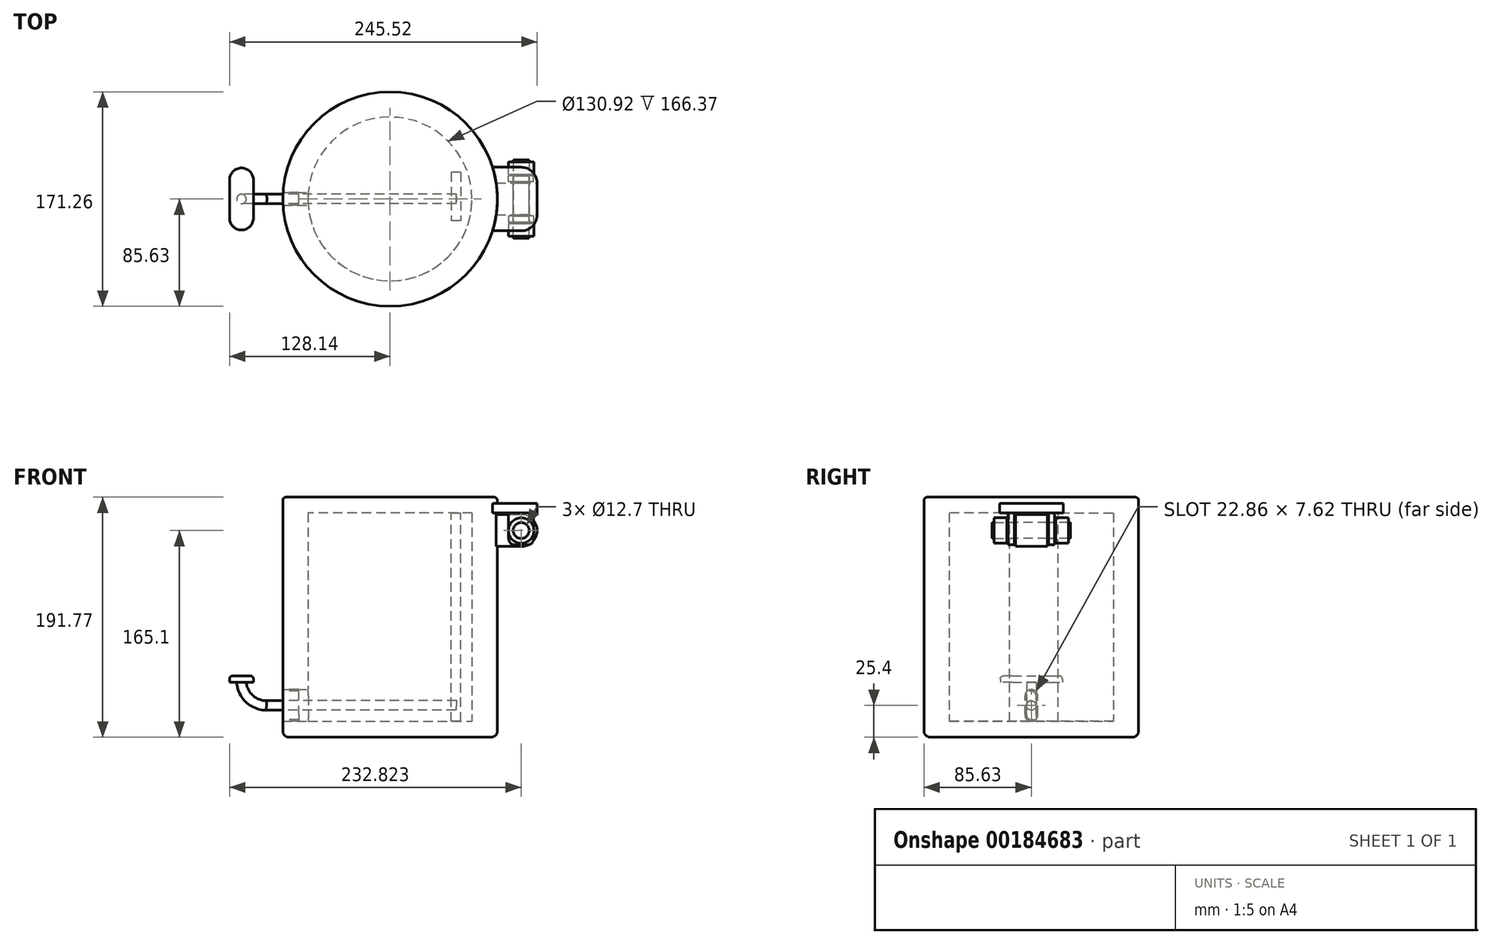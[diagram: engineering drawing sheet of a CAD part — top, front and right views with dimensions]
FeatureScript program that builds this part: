
annotation { "Feature Type Name" : "Feature", "Feature Type Description" : "" }
export const myFeature = defineFeature(function(context is Context, id is Id, definition is map)
    precondition{}
    {
        {
            var Q0;
            Q0=qCreatedBy(makeId("Top.planeOp"),FACE);
            var sketch = newSketch(context, id + "F0", { "sketchPlane" : qUnion([Q0])});
            skCircle(sketch, "E0", {"center": v(0, 0) * mm, "radius": 85.63 * mm});
            skCircle(sketch, "E1", {"center": v(0, 0) * mm, "radius": 65.46 * mm});
            skSolve(sketch);
        }
        {
            var Q0;
            Q0 = qSketchRegion(id + "F0", true);
            extrude(context, id + "F1", {"entities" : qUnion([Q0]), "depth" : 177.8 * mm});
        }
        {
            var Q0;
            Q0=makeQuery(id+"F0.imprint","IMPRINT",FACE,{"disambiguationData":[TD([[makeQuery(id+"F0.imprint","IMPRINT",EDGE,{"derivedFrom":sQuery(id+"F0.wireOp",EDGE,"E0")}),1.0]])]});
            var Q1;
            Q1=makeQuery(id+"F0.imprint","IMPRINT",FACE,{"disambiguationData":[TD([[makeQuery(id+"F0.imprint","IMPRINT",EDGE,{"derivedFrom":sQuery(id+"F0.wireOp",EDGE,"E1")}),1.0]])]});
            extrude(context, id + "F2", {"entities" : qUnion([Q0, Q1]), "operationType" : NewBodyOperationType.ADD, "depth" : 12.7 * mm});
        }
        {
            var Q0;
            Q0=makeQuery(id+"F1.opExtrude","CAP_FACE",FACE,{"disambiguationData":[OSD([sQuery(id+"F0.wireOp",EDGE,"E0"),sQuery(id+"F0.wireOp",EDGE,"E1")])],"isStart":false});
            var sketch = newSketch(context, id + "F3", { "sketchPlane" : qUnion([Q0])});
            skCircle(sketch, "E2.0", {"center": v(0, 0) * mm, "radius": 85.63 * mm});
            skCircle(sketch, "E2.1", {"center": v(0, 0) * mm, "radius": 65.46 * mm});
            skSolve(sketch);
        }
        {
            var Q0;
            Q0 = qSketchRegion(id + "F3", true);
            extrude(context, id + "F4", {"entities" : qUnion([Q0]), "depth" : 1.27 * mm});
        }
        {
            var Q0;
            Q0=makeQuery(id+"F4.opExtrude","CAP_FACE",FACE,{"disambiguationData":[OSD([sQuery(id+"F3.wireOp",EDGE,"E2.0"),sQuery(id+"F3.wireOp",EDGE,"E2.1")])],"isStart":false});
            var sketch = newSketch(context, id + "F5", { "sketchPlane" : qUnion([Q0])});
            skCircle(sketch, "E3.0", {"center": v(0, 0) * mm, "radius": 85.63 * mm});
            skSolve(sketch);
        }
        {
            var Q0;
            Q0 = qSketchRegion(id + "F5", true);
            extrude(context, id + "F6", {"entities" : qUnion([Q0]), "depth" : 12.7 * mm});
        }
        {
            var Q0;
            Q0=makeQuery(id+"F6.opExtrude","CAP_EDGE",EDGE,{"disambiguationData":[OSD([sQuery(id+"F5.wireOp",EDGE,"E3.0")])],"isStart":false});
            fillet(context, id + "F7", {"entities" : qUnion([Q0]), "radius" : 2.54 * mm, "tangentPropagation" : true, "allowEdgeOverflow" : false});
        }
        {
            var Q0;
            Q0=makeQuery(id+"F1.opExtrude","CAP_EDGE",EDGE,{"disambiguationData":[OSD([sQuery(id+"F0.wireOp",EDGE,"E0")])],"isStart":true});
            fillet(context, id + "F8", {"entities" : qUnion([Q0]), "radius" : 5.08 * mm, "tangentPropagation" : true, "allowEdgeOverflow" : false});
        }
        {
            var Q0;
            Q0=makeQuery(id+"F6.opExtrude","CAP_FACE",FACE,{"disambiguationData":[OSD([sQuery(id+"F5.wireOp",EDGE,"E3.0")])],"isStart":true});
            var sketch = newSketch(context, id + "F9", { "sketchPlane" : qUnion([Q0])});
            skLineSegment(sketch, "E4.bottom", {"start": v(48.96, 17.22) * mm, "end": v(56.36, 17.22) * mm});
            skLineSegment(sketch, "E4.top", {"start": v(48.96, -21.27) * mm, "end": v(56.36, -21.27) * mm});
            skLineSegment(sketch, "E4.left", {"start": v(48.96, 17.22) * mm, "end": v(48.96, -21.27) * mm});
            skLineSegment(sketch, "E4.right", {"start": v(56.36, 17.22) * mm, "end": v(56.36, -21.27) * mm});
            skSolve(sketch);
        }
        {
            var Q0;
            Q0 = qSketchRegion(id + "F9", true);
            extrude(context, id + "F10", {"entities" : qUnion([Q0]), "endBound" : BoundingType.UP_TO_NEXT, "depth" : 132.08 * mm});
        }
        {
            var Q0;
            Q0=qCreatedBy(makeId("Right.planeOp"),FACE);
            var sketch = newSketch(context, id + "F11", { "sketchPlane" : qUnion([Q0])});
            skLineSegment(sketch, "E5.0", {"start": v(-85.63, 179.07) * mm, "end": v(85.63, 179.07) * mm});
            skLineSegment(sketch, "E5.1", {"start": v(-85.63, 177.8) * mm, "end": v(85.63, 177.8) * mm});
            skLineSegment(sketch, "E6", {"start": v(0, 45.64) * mm, "end": v(0, -59.13) * mm});
            skPoint(sketch, "E6.startSnap0", {"position": v(0, 177.8) * mm});
            skLineSegment(sketch, "E7.bottom", {"start": v(-5.08, 17.78) * mm, "end": v(5.08, 17.78) * mm});
            skLineSegment(sketch, "E7.top", {"start": v(-5.08, 33.02) * mm, "end": v(5.08, 33.02) * mm});
            skLineSegment(sketch, "E7.left", {"start": v(-5.08, 17.78) * mm, "end": v(-5.08, 33.02) * mm});
            skLineSegment(sketch, "E7.right", {"start": v(5.08, 17.78) * mm, "end": v(5.08, 33.02) * mm});
            skPoint(sketch, "E7.middle", {"position": v(0, 25.4) * mm});
            skArc(sketch, "E8", {"start": v(5.08, 33.02) * mm, "mid": v(0, 38.1) * mm, "end": v(-5.08, 33.02) * mm});
            skArc(sketch, "E9", {"start": v(-5.08, 17.78) * mm, "mid": v(0, 12.7) * mm, "end": v(5.08, 17.78) * mm});
            skSolve(sketch);
        }
        {
            var Q0;
            Q0 = qSketchRegion(id + "F11", true);
            extrude(context, id + "F12", {"entities" : qUnion([Q0]), "operationType" : NewBodyOperationType.REMOVE, "endBound" : BoundingType.THROUGH_ALL, "oppositeDirection" : true, "depth" : 25.4 * mm});
        }
        {
            var Q0;
            Q0=qCreatedBy(makeId("Front.planeOp"),FACE);
            var sketch = newSketch(context, id + "F13", { "sketchPlane" : qUnion([Q0])});
            skFitSpline(sketch, "E10.0", {"points": [v(-85.48, 17.78) * mm, v(-85.48, 17.78) * mm, v(-85.48, 17.72) * mm, v(-85.46, 17.52) * mm, v(-85.44, 17.23) * mm, v(-85.41, 16.75) * mm, v(-85.37, 16.08) * mm, v(-85.34, 15.47) * mm, v(-85.32, 14.97) * mm, v(-85.3, 14.43) * mm, v(-85.28, 13.87) * mm, v(-85.27, 13.28) * mm, v(-85.26, 12.67) * mm, v(-85.25, 12.06) * mm, v(-85.25, 11.44) * mm, v(-85.25, 10.81) * mm, v(-85.26, 9.98) * mm, v(-85.27, 9.2) * mm, v(-85.3, 8.43) * mm, v(-85.32, 7.9) * mm, v(-85.34, 7.4) * mm, v(-85.36, 6.94) * mm, v(-85.39, 6.52) * mm, v(-85.4, 6.15) * mm, v(-85.43, 5.83) * mm, v(-85.45, 5.47) * mm, v(-85.48, 5.17) * mm, v(-85.48, 5.08) * mm, v(-85.48, 5.08) * mm, v(-85.48, 17.78) * mm]});
            skLineSegment(sketch, "E11", {"start": v(-98.6, 25.4) * mm, "end": v(52.86, 25.4) * mm});
            skPoint(sketch, "E11.startSnap0", {"position": v(-85.63, 25.4) * mm});
            skArc(sketch, "E12", {"start": v(-118.61, 44.06) * mm, "mid": v(-112.28, 30.79) * mm, "end": v(-98.6, 25.4) * mm});
            skSolve(sketch);
        }
        {
            var Q0;
            Q0=qCreatedBy(makeId("Top.planeOp"),FACE);
            var Q1;
            Q1=sQuery(id+"F13.wireOp",VERTEX,"E12.start");
            cPlane(context, id + "F14", {"entities" : qUnion([Q0, Q1]), "cplaneType" : CPlaneType.PLANE_POINT, "offset" : 25.4 * mm, "width" : 152.4 * mm, "height" : 152.4 * mm});
        }
        {
            var Q0;
            Q0=qCreatedBy(id+"F14.planeOp",FACE);
            var sketch = newSketch(context, id + "F15", { "sketchPlane" : qUnion([Q0])});
            skPoint(sketch, "E13.0", {"position": v(-118.61, 0) * mm});
            skCircle(sketch, "E14", {"center": v(-118.61, 0) * mm, "radius": 3.8 * mm});
            skSolve(sketch);
        }
        {
            var Q0;
            Q0=makeQuery(id+"F15.imprint","IMPRINT",FACE,{"disambiguationData":[TD([[makeQuery(id+"F15.imprint","IMPRINT",EDGE,{"derivedFrom":sQuery(id+"F15.wireOp",EDGE,"E14")}),1.0]])]});
            var Q1;
            Q1=sQuery(id+"F13.wireOp",EDGE,"E12");
            var Q2;
            Q2=sQuery(id+"F13.wireOp",EDGE,"E11");
            sweep(context, id + "F16", {"profiles" : qUnion([Q0]), "path" : qUnion([Q1, Q2])});
        }
        {
            var Q0;
            Q0=makeQuery(id+"F16.opSweep","CAP_FACE",FACE,{"disambiguationData":[OSD([sQuery(id+"F13.wireOp",VERTEX,"E12.start"),sQuery(id+"F15.wireOp",EDGE,"E14")])],"isStart":true});
            var sketch = newSketch(context, id + "F17", { "sketchPlane" : qUnion([Q0])});
            skCircle(sketch, "E15.0", {"center": v(-118.61, 0) * mm, "radius": 3.8 * mm});
            skLineSegment(sketch, "E16.bottom", {"start": v(-109.09, -15.24) * mm, "end": v(-128.14, -15.24) * mm});
            skLineSegment(sketch, "E16.top", {"start": v(-109.09, 15.24) * mm, "end": v(-128.14, 15.24) * mm});
            skLineSegment(sketch, "E16.left", {"start": v(-109.09, -15.24) * mm, "end": v(-109.09, 15.24) * mm});
            skLineSegment(sketch, "E16.right", {"start": v(-128.14, -15.24) * mm, "end": v(-128.14, 15.24) * mm});
            skArc(sketch, "E17", {"start": v(-109.09, 15.24) * mm, "mid": v(-118.61, 24.77) * mm, "end": v(-128.14, 15.24) * mm});
            skArc(sketch, "E18", {"start": v(-128.14, -15.24) * mm, "mid": v(-118.61, -24.77) * mm, "end": v(-109.09, -15.24) * mm});
            skSolve(sketch);
        }
        {
            var Q0;
            Q0=makeQuery(id+"F17.imprint","IMPRINT",FACE,{"disambiguationData":[TD([[makeQuery(id+"F17.imprint","IMPRINT",EDGE,{"derivedFrom":sQuery(id+"F17.wireOp",EDGE,"E15.0")}),1.0]])]});
            var Q1;
            Q1=makeQuery(id+"F17.imprint","IMPRINT",FACE,{"disambiguationData":[TD([[makeQuery(id+"F17.imprint","IMPRINT",EDGE,{"derivedFrom":sQuery(id+"F17.wireOp",EDGE,"E16.top")}),-1.0]])]});
            var Q2;
            Q2=makeQuery(id+"F17.imprint","IMPRINT",FACE,{"disambiguationData":[TD([[makeQuery(id+"F17.imprint","IMPRINT",EDGE,{"derivedFrom":sQuery(id+"F17.wireOp",EDGE,"E16.bottom")}),1.0]])]});
            var Q3;
            Q3=makeQuery(id+"F17.imprint","IMPRINT",FACE,{"disambiguationData":[TD([[makeQuery(id+"F17.imprint","IMPRINT",EDGE,{"derivedFrom":sQuery(id+"F17.wireOp",EDGE,"E15.0")}),-1.0]])]});
            extrude(context, id + "F18", {"entities" : qUnion([Q0, Q1, Q2, Q3]), "operationType" : NewBodyOperationType.ADD, "depth" : 5.08 * mm});
        }
        {
            var Q0;
            Q0=makeQuery(id+"F18.opExtrude","CAP_EDGE",EDGE,{"disambiguationData":[OSD([sQuery(id+"F17.wireOp",EDGE,"E16.left")])],"isStart":false});
            fillet(context, id + "F19", {"entities" : qUnion([Q0]), "radius" : 2.54 * mm, "tangentPropagation" : true, "allowEdgeOverflow" : false});
        }
        {
            var Q0;
            Q0=makeQuery(id+"F12.boolean.opBoolean","INTERSECT",EDGE,{"derivedFrom":[makeQuery(id+"F1.opExtrude","SWEPT_FACE",FACE,{"disambiguationData":[OSD([sQuery(id+"F0.wireOp",EDGE,"E0")])]}),makeQuery(id+"F12.opExtrude","SWEPT_FACE",FACE,{"disambiguationData":[OSD([sQuery(id+"F11.wireOp",EDGE,"E9")])]})]});
            cPoint(context, id + "F20", {"entities" : qUnion([Q0]), "parameter" : 0.5});
        }
        {
            var Q0;
            Q0=qCreatedBy(makeId("Right.planeOp"),FACE);
            var Q1;
            Q1 = qCreatedBy(id + "F20" ,VERTEX);
            cPlane(context, id + "F21", {"entities" : qUnion([Q0, Q1]), "cplaneType" : CPlaneType.PLANE_POINT, "offset" : 25.4 * mm, "width" : 152.4 * mm, "height" : 152.4 * mm});
        }
        {
            var Q0;
            Q0=qCreatedBy(id+"F21.planeOp",FACE);
            var sketch = newSketch(context, id + "F22", { "sketchPlane" : qUnion([Q0])});
            skLineSegment(sketch, "E19.0", {"start": v(-5.08, 17.78) * mm, "end": v(-5.08, 33.02) * mm});
            skArc(sketch, "E19.1", {"start": v(-5.08, 17.78) * mm, "mid": v(0, 12.7) * mm, "end": v(5.08, 17.78) * mm});
            skLineSegment(sketch, "E19.2", {"start": v(5.08, 17.78) * mm, "end": v(5.08, 33.02) * mm});
            skArc(sketch, "E19.3", {"start": v(5.08, 33.02) * mm, "mid": v(0, 38.1) * mm, "end": v(-5.08, 33.02) * mm});
            skLineSegment(sketch, "E20.0", {"start": v(-3.8, 17.78) * mm, "end": v(-3.8, 33.02) * mm});
            skArc(sketch, "E20.1", {"start": v(-3.81, 17.78) * mm, "mid": v(0, 13.97) * mm, "end": v(3.8, 17.78) * mm});
            skLineSegment(sketch, "E20.2", {"start": v(3.8, 17.78) * mm, "end": v(3.8, 33.02) * mm});
            skArc(sketch, "E20.3", {"start": v(3.8, 33.02) * mm, "mid": v(0, 36.83) * mm, "end": v(-3.81, 33.02) * mm});
            skSolve(sketch);
        }
        {
            var Q0;
            Q0 = qSketchRegion(id + "F22", true);
            extrude(context, id + "F23", {"entities" : qUnion([Q0]), "depth" : 12.7 * mm});
        }
        {
            var Q0;
            Q0=qCreatedBy(makeId("Front.planeOp"),FACE);
            var sketch = newSketch(context, id + "F24", { "sketchPlane" : qUnion([Q0])});
            skLineSegment(sketch, "E21.0", {"start": v(-85.63, 177.8) * mm, "end": v(85.63, 177.8) * mm});
            skLineSegment(sketch, "E22", {"start": v(85.63, 177.8) * mm, "end": v(85.63, 8.1) * mm});
            skCircle(sketch, "E23", {"center": v(104.68, 165.1) * mm, "radius": 12.7 * mm});
            skCircle(sketch, "E24", {"center": v(104.68, 165.1) * mm, "radius": 6.35 * mm});
            skLineSegment(sketch, "E25", {"start": v(104.68, 177.8) * mm, "end": v(85.63, 177.8) * mm});
            skLineSegment(sketch, "E26", {"start": v(104.68, 152.4) * mm, "end": v(85.63, 152.4) * mm});
            skLineSegment(sketch, "E27", {"start": v(104.68, 177.8) * mm, "end": v(79.9, 177.8) * mm});
            skLineSegment(sketch, "E28", {"start": v(79.9, 177.8) * mm, "end": v(79.9, 152.4) * mm});
            skLineSegment(sketch, "E29", {"start": v(79.9, 152.4) * mm, "end": v(104.68, 152.4) * mm});
            skSolve(sketch);
        }
        {
            var Q0;
            Q0 = qSketchRegion(id + "F24", true);
            extrude(context, id + "F25", {"entities" : qUnion([Q0]), "operationType" : NewBodyOperationType.ADD, "endBound" : BoundingType.SYMMETRIC, "depth" : 25.4 * mm});
        }
        {
            var Q0;
            Q0=makeQuery(id+"F6.opExtrude","CAP_FACE",FACE,{"disambiguationData":[OSD([sQuery(id+"F5.wireOp",EDGE,"E3.0")])],"isStart":false});
            cPlane(context, id + "F26", {"entities" : qUnion([Q0]), "cplaneType" : CPlaneType.OFFSET, "offset" : 5.08 * mm, "oppositeDirection" : true, "width" : 152.4 * mm, "height" : 152.4 * mm});
        }
        {
            var Q0;
            Q0=qCreatedBy(id+"F26.planeOp",FACE);
            var sketch = newSketch(context, id + "F27", { "sketchPlane" : qUnion([Q0])});
            skLineSegment(sketch, "E30.0", {"start": v(117.38, -25.4) * mm, "end": v(84.69, -25.4) * mm});
            skLineSegment(sketch, "E30.1", {"start": v(117.38, -25.4) * mm, "end": v(117.38, 25.4) * mm});
            skLineSegment(sketch, "E30.2", {"start": v(117.38, 25.4) * mm, "end": v(84.69, 25.4) * mm});
            skLineSegment(sketch, "E31", {"start": v(84.69, -25.4) * mm, "end": v(75.68, -25.4) * mm});
            skLineSegment(sketch, "E32", {"start": v(84.69, 25.4) * mm, "end": v(75.45, 25.4) * mm});
            skLineSegment(sketch, "E33", {"start": v(75.45, 25.4) * mm, "end": v(75.68, -25.4) * mm});
            skSolve(sketch);
        }
        {
            var Q0;
            Q0 = qSketchRegion(id + "F27", true);
            extrude(context, id + "F28", {"entities" : qUnion([Q0]), "operationType" : NewBodyOperationType.ADD, "oppositeDirection" : true, "depth" : 7.62 * mm});
        }
        {
            var Q0;
            Q0=makeQuery(id+"F28.opExtrude","SWEPT_EDGE",EDGE,{"disambiguationData":[OSD([sQuery(id+"F27.wireOp",EDGE,"E30.1"),sQuery(id+"F27.wireOp",EDGE,"E30.2")])]});
            var Q1;
            Q1=makeQuery(id+"F28.opExtrude","SWEPT_EDGE",EDGE,{"disambiguationData":[OSD([sQuery(id+"F27.wireOp",EDGE,"E30.0"),sQuery(id+"F27.wireOp",EDGE,"E30.1")])]});
            fillet(context, id + "F29", {"entities" : qUnion([Q0, Q1]), "radius" : 12.7 * mm, "tangentPropagation" : true, "allowEdgeOverflow" : false});
        }
        {
            var Q0;
            Q0=makeQuery(id+"F28.opExtrude","CAP_FACE",FACE,{"disambiguationData":[OSD([sQuery(id+"F27.wireOp",EDGE,"E30.0"),sQuery(id+"F27.wireOp",EDGE,"E30.1"),sQuery(id+"F27.wireOp",EDGE,"E30.2"),sQuery(id+"F27.wireOp",EDGE,"E31"),sQuery(id+"F27.wireOp",EDGE,"E32"),sQuery(id+"F27.wireOp",EDGE,"E33")])],"isStart":false});
            var sketch = newSketch(context, id + "F30", { "sketchPlane" : qUnion([Q0])});
            skLineSegment(sketch, "E34.0", {"start": v(84.69, -12.7) * mm, "end": v(104.68, -12.7) * mm});
            skLineSegment(sketch, "E34.1", {"start": v(84.69, 12.7) * mm, "end": v(104.68, 12.7) * mm});
            skLineSegment(sketch, "E35.0", {"start": v(98.33, -12.7) * mm, "end": v(111.03, -12.7) * mm});
            skLineSegment(sketch, "E36.bottom", {"start": v(114.7, -13.63) * mm, "end": v(94.68, -13.63) * mm});
            skLineSegment(sketch, "E36.top", {"start": v(114.7, -18.53) * mm, "end": v(94.68, -18.53) * mm});
            skLineSegment(sketch, "E36.left", {"start": v(114.7, -13.63) * mm, "end": v(114.7, -18.53) * mm});
            skLineSegment(sketch, "E36.right", {"start": v(94.68, -13.63) * mm, "end": v(94.68, -18.53) * mm});
            skPoint(sketch, "E36.middle", {"position": v(104.68, -16.08) * mm});
            skLineSegment(sketch, "E37", {"start": v(111.03, -13.63) * mm, "end": v(111.03, -18.53) * mm});
            skLineSegment(sketch, "E38", {"start": v(98.33, -13.63) * mm, "end": v(98.33, -18.53) * mm});
            skLineSegment(sketch, "E39.0", {"start": v(104.68, 12.7) * mm, "end": v(104.68, -12.7) * mm});
            skLineSegment(sketch, "E40", {"start": v(122.8, 0) * mm, "end": v(89.7, 0) * mm, "construction": true});
            skPoint(sketch, "E40.startSnap0", {"position": v(117.38, 0) * mm});
            skPoint(sketch, "E40.endSnap0", {"position": v(117.38, 0) * mm});
            skPoint(sketch, "E41.MirrorP", {"position": v(104.68, 16.08) * mm});
            skLineSegment(sketch, "E42.MirrorCS", {"start": v(98.33, 13.63) * mm, "end": v(98.33, 18.53) * mm});
            skLineSegment(sketch, "E43.MirrorCS", {"start": v(111.03, 13.63) * mm, "end": v(111.03, 18.53) * mm});
            skLineSegment(sketch, "E44.MirrorCS", {"start": v(114.7, 13.63) * mm, "end": v(94.68, 13.63) * mm});
            skLineSegment(sketch, "E45.MirrorCS", {"start": v(94.68, 13.63) * mm, "end": v(94.68, 18.53) * mm});
            skLineSegment(sketch, "E46.MirrorCS", {"start": v(114.7, 13.63) * mm, "end": v(114.7, 18.53) * mm});
            skLineSegment(sketch, "E47.MirrorCS", {"start": v(98.33, 12.7) * mm, "end": v(111.03, 12.7) * mm});
            skLineSegment(sketch, "E48.MirrorCS", {"start": v(114.7, 18.53) * mm, "end": v(94.68, 18.53) * mm});
            skSolve(sketch);
        }
        {
            var Q0;
            Q0 = qSketchRegion(id + "F30", true);
            extrude(context, id + "F31", {"entities" : qUnion([Q0]), "operationType" : NewBodyOperationType.ADD, "depth" : 25.4 * mm});
        }
        {
            var Q0;
            Q0=makeQuery(id+"F31.opExtrude","SWEPT_FACE",FACE,{"disambiguationData":[OSD([sQuery(id+"F30.wireOp",EDGE,"E36.top")])]});
            var sketch = newSketch(context, id + "F32", { "sketchPlane" : qUnion([Q0])});
            skCircle(sketch, "E49.0", {"center": v(-104.68, 165.1) * mm, "radius": 6.35 * mm});
            skSolve(sketch);
        }
        {
            var Q0;
            Q0 = qSketchRegion(id + "F32", true);
            extrude(context, id + "F33", {"entities" : qUnion([Q0]), "operationType" : NewBodyOperationType.REMOVE, "endBound" : BoundingType.THROUGH_ALL, "oppositeDirection" : true, "depth" : 25.4 * mm});
        }
        {
            var Q0;
            Q0=makeQuery(id+"F31.opExtrude","CAP_EDGE",EDGE,{"disambiguationData":[OSD([sQuery(id+"F30.wireOp",EDGE,"E36.left")])],"isStart":false});
            var Q1;
            Q1=makeQuery(id+"F31.opExtrude","CAP_EDGE",EDGE,{"disambiguationData":[OSD([sQuery(id+"F30.wireOp",EDGE,"E36.right")])],"isStart":false});
            var Q2;
            Q2=makeQuery(id+"F31.opExtrude","CAP_EDGE",EDGE,{"disambiguationData":[OSD([sQuery(id+"F30.wireOp",EDGE,"E46.MirrorCS")])],"isStart":false});
            var Q3;
            Q3=makeQuery(id+"F31.opExtrude","CAP_EDGE",EDGE,{"disambiguationData":[OSD([sQuery(id+"F30.wireOp",EDGE,"E45.MirrorCS")])],"isStart":false});
            fillet(context, id + "F34", {"entities" : qUnion([Q0, Q1, Q2, Q3]), "radius" : 5.08 * mm, "tangentPropagation" : true, "allowEdgeOverflow" : false});
        }
        {
            var Q0;
            Q0=makeQuery(id+"F31.opExtrude","SWEPT_FACE",FACE,{"disambiguationData":[OSD([sQuery(id+"F30.wireOp",EDGE,"E36.top")])]});
            var sketch = newSketch(context, id + "F35", { "sketchPlane" : qUnion([Q0])});
            skCircle(sketch, "E50.0", {"center": v(-104.68, 165.1) * mm, "radius": 6.35 * mm});
            skSolve(sketch);
        }
        {
            var Q0;
            Q0 = qSketchRegion(id + "F35", true);
            extrude(context, id + "F36", {"entities" : qUnion([Q0]), "depth" : 12.7 * mm, "hasSecondDirection" : true, "secondDirectionOppositeDirection" : true, "secondDirectionDepth" : 48.26 * mm});
        }
        {
            var Q0;
            Q0=makeQuery(id+"F36.opExtrude","CAP_FACE",FACE,{"disambiguationData":[OSD([sQuery(id+"F35.wireOp",EDGE,"E50.0")])],"isStart":true});
            var sketch = newSketch(context, id + "F37", { "sketchPlane" : qUnion([Q0])});
            skCircle(sketch, "E51", {"center": v(104.68, 165.1) * mm, "radius": 10.16 * mm});
            skSolve(sketch);
        }
        {
            var Q0;
            Q0 = qSketchRegion(id + "F37", true);
            extrude(context, id + "F38", {"entities" : qUnion([Q0]), "operationType" : NewBodyOperationType.ADD, "oppositeDirection" : true, "depth" : 10.16 * mm});
        }
        {
            var Q0;
            Q0=makeQuery(id+"F36.opExtrude","SWEPT_BODY",BODY,{"disambiguationData":[OSD([sQuery(id+"F35.wireOp",EDGE,"E50.0")])]});
            var Q1;
            Q1=qCreatedBy(makeId("Front.planeOp"),FACE);
            mirror(context, id + "F39", {"entities" : qUnion([Q0]), "mirrorPlane" : qUnion([Q1])});
        }
    });
